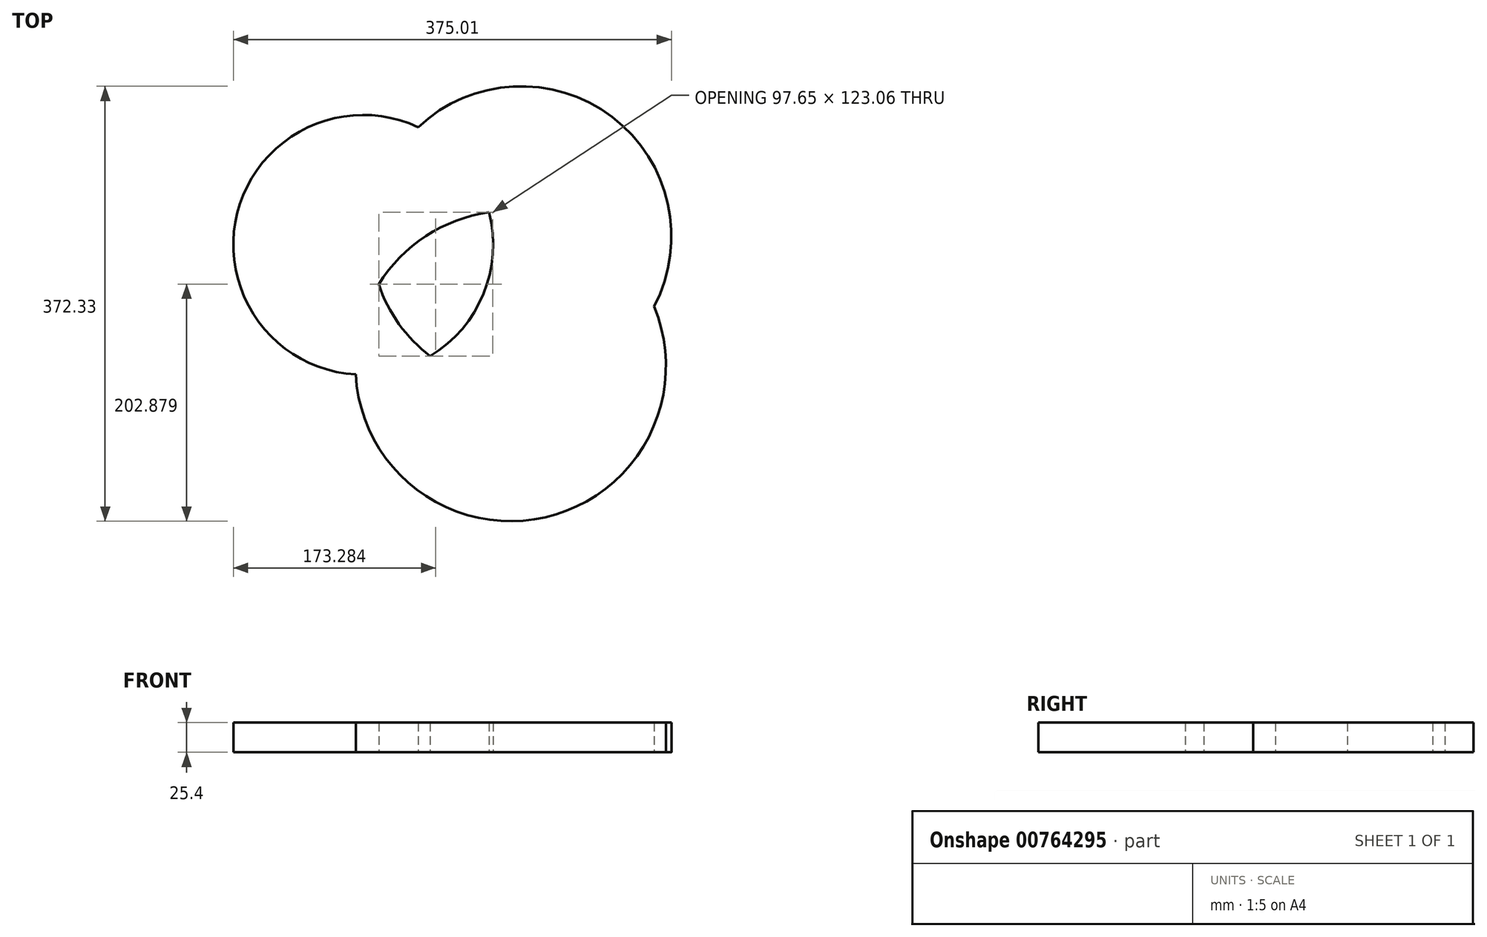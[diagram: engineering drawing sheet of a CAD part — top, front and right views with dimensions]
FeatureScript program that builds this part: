
annotation { "Feature Type Name" : "Feature", "Feature Type Description" : "" }
export const myFeature = defineFeature(function(context is Context, id is Id, definition is map)
    precondition{}
    {
        {
            var Q0;
            Q0=qCreatedBy(makeId("Top.planeOp"),FACE);
            var sketch = newSketch(context, id + "F0", { "sketchPlane" : qUnion([Q0])});
            skCircle(sketch, "E0", {"center": v(-193.67, 8.24) * mm, "radius": 128.62 * mm});
            skPoint(sketch, "E0.first.point", {"position": v(-85.2, -60.87) * mm});
            skPoint(sketch, "E0.second.point", {"position": v(-322.02, 0) * mm});
            skPoint(sketch, "E0.third.point", {"position": v(-242.14, -110.9) * mm});
            skCircle(sketch, "E1", {"center": v(-202.64, -102.61) * mm, "radius": 132.86 * mm});
            skPoint(sketch, "E1.first.point", {"position": v(-214.4, 29.72) * mm});
            skPoint(sketch, "E1.second.point", {"position": v(-200.13, -235.45) * mm});
            skPoint(sketch, "E1.third.point", {"position": v(-335.3, -109.86) * mm});
            skCircle(sketch, "E2", {"center": v(-328.88, 1.14) * mm, "radius": 111.18 * mm});
            skPoint(sketch, "E2.second.point", {"position": v(-394.32, 91.02) * mm});
            skPoint(sketch, "E2.third.point", {"position": v(-385.28, 96.95) * mm});
            skSolve(sketch);
        }
        {
            var Q0;
            {var subQ0=sQuery(id+"F0.wireOp",EDGE,"E2");var subQ1=sQuery(id+"F0.wireOp",EDGE,"E0");var subQ2=makeQuery(id+"F0.imprint","INTERSECT",VERTEX,{"disambiguationData":[OD(0.0)],"derivedFrom":[subQ1,subQ0]});Q0=makeQuery(id+"F0.imprint","IMPRINT",FACE,{"disambiguationData":[TD([[makeQuery(id+"F0.imprint","IMPRINT",EDGE,{"disambiguationData":[TD([[subQ2,-1.0]])],"derivedFrom":subQ1}),-1.0]])]});}
            extrude(context, id + "F1", {"entities" : qUnion([Q0]), "depth" : 25.4 * mm, "offsetDistance" : 25.4 * mm});
        }
        {
            var Q0;
            Q0 = qSketchRegion(id + "F0", true);
            extrude(context, id + "F2", {"entities" : qUnion([Q0]), "operationType" : NewBodyOperationType.ADD, "depth" : 25.4 * mm, "offsetDistance" : 25.4 * mm});
        }
    });
